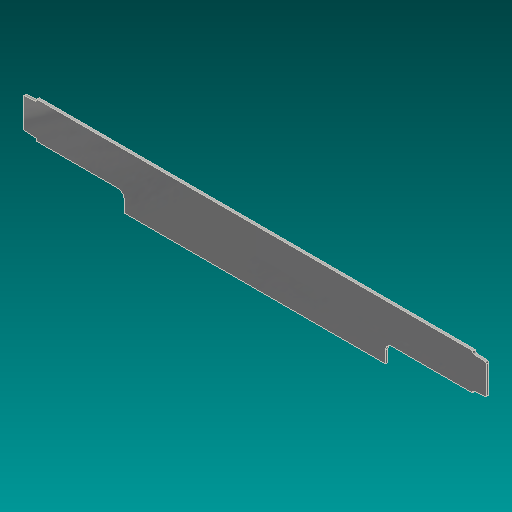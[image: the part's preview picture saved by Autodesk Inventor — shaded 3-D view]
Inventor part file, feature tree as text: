
AUTODESK INVENTOR PART (.ipt)
format: ipt  version: 2017 (Build 210142000, 142)  size: 121,856 bytes
history: native  units: in
note: dims shown in document units (in); Inventor stores cm internally (conversion verified against a paired STEP export)
features: extrude x1, fillet x1
ambient origin geometry x8: Origin, YZ Plane, XZ Plane, XY Plane, X Axis, Y Axis, Z Axis, Center Point
bodies: Solid1 (feature_tree)
feature tree (2):
  extrude  "Extrusion1"  Depth=26.75in
  fillet  "Fillet1"  Radius=47.375in
